# Revit family: KEUCO_53909010000
name_source: partatom
category: Sanitärinstallationen
revit_build: Autodesk Revit 2016 (Build: 20150220_1215(x64)
units: mm (PartAtom-declared; Revit-internal decimal feet)

## family parameters
Arbeitsebenenbasiert = Ja
Beim Laden mit Abzugskörper schneiden = Nein
Bemaßung runder Anschluss = Durchmesser verwenden
Gemeinsam genutzt = Nein
Immer vertikal = Ja
OmniClass-Nummer = 23.45.00.00
Raumberechnungspunkt = Nein
Teiletyp = Normal

## types (1)
- 53909010000
    Artikelnummer = 53909010000
    Ausschreibungstext = KEUCO PLAN blue Einhebel-Bidetmischer 53909010000
hochglanzverchromter Einhebel Bidetmischer 
in ästhetischem, funktionalem Design, 
für Standmontage, 
inklusive Zugstangen-Ablaufgarnitur,
hochwertige Mischwasserkartusche mit 
keramischen Dichtscheiben und Temperaturbegrenzung,
Durchflussmenge begrenzt auf 6 l/min.,
Betätigungselement aus Metall,
Einlochmontage mit Schnell-Montage-System,
Luftsprudler M24x1, mit Kugelgelenk bis 25° neigbar,
Höhe 136 mm, Auslaufhöhe 19 mm, Ausladung 138 mm,
Grundkörperdurchmesser 48 mm, Auslaufdurchmesser 28 mm
Wasseranschluss mit flexiblen Druckschläuchen, 
Länge 420 mm, Gewindedurchmesser G 3/8 Zoll,
Anschlussrohrlänge 350 mm,
Zugstangen-Ablaufgarnitur 
mit G 1 1/4 Zoll Anschlussgewinde,
Länge der Zugstange 400 mm,
Abdeckstopfen Durchmesser 63 mm
DVGW geprüft
    Beschreibung = mit Zugstangen-Ablaufgarnitur 1 1/4 Zoll
Einlochmontage mit Schnell-Montage-System
Mischwasserkartusche mit keramischen Dichtscheiben
und Temperaturbegrenzung,
Luftsprudler M 24x1, mit Kugelgelenk
Druckschläuche 420 mm G 3/8 Zoll
Durchflussmenge begrenzt auf 7,6 l/min.
geräuschgeprüft
    Breite = 111 mm
    Gewicht = 858
    Hersteller = KEUCO
    Kategorie = ARM
    Material Wasserhahn = 23589001 Chrome
    Preisgruppe = 1
    URL = https://www.keuco.com
    Verwendung = GWC / WP
    Vorgabe-Ansicht = 1219 mm

## geometry (parser evidence)
native form markers: Sweep x2
no freeform markers — native parametric forms only
